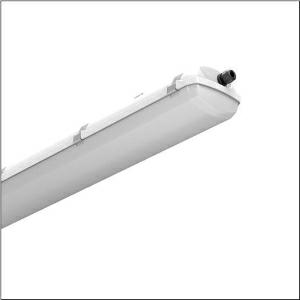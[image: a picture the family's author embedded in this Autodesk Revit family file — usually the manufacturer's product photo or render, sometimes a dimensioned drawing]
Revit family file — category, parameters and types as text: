
# Revit family: monsun_r__ex_51fxa27l460a_7d1b
name_source: partatom
category: Lighting Fixtures
units: mm (PartAtom-declared; Revit-internal decimal feet)

## family parameters
Cut with Voids When Loaded = No
Host = Face
Light Source = No
Part Type = Normal
Room Calculation Point = No
Round Connector Dimension = Use Diameter
Shared = No

## types (1)
- Monsun® Ex (1 x LED, 6560 lm, 53 W, 4000K)
    Apparent Load = 53 VA
    CIE Flux Codes = 46 76 94 98 100
    Color Rendering = 80
    Color Temperature = 4000K
    Default Elevation = 1800 mm
    Description = Monsun® Ex, damp-proof luminaire, primary optical cover: cover, of PC, UV-stabilised, opal, light emission: direct distribution, primary light characteristic: symmetric, installation type: surface-mounted, LED, rated luminous flux: 6.560lm, luminous efficacy: 124lm/W, light colour: 840, colour temperature: 4000K, control gear: ON/OFF, with terminal, 3-pole, max. 2.5mm², through-wiring: 5x 2.5mm², mains connection: 220..250V, AC, 50/60Hz, rated input power: 53W, housing, of PC, light grey (RAL 7035), incl. 1x Ex cable gland M20 for cable diameter 7..12mm with sealing, incl. 1x Ex locking screw M20 with sealing, length: 1.280mm, width: 155mm, height: 105mm, clip for enclosure, of stainless steel, protection rating (complete): IP66, insulation class (complete): insulation class I (protective earthing), certification: CE, explosion class: zone 1,21 II 2G Ex eb mb op is IIC T4 Gb, II 2D Ex tb op is IIIC T67°C Db, impact resistance: IK10, permissible operating ambient temperature: -20..+40°C, contact your sales advisor before using the luminaires in applications with unclear chemical exposure, large temperature fluctuations or condensation-forming humidity, packaging unit: 1 piece
    Height = 105 mm
    Lamp = 1 x LED
    Lamp Light Flux = 6560 lm
    Lamp Power = 53 W
    Lamp count = 1
    Length = 1280 mm
    Luminous efficacy = 124 lm/W
    Manufacturer = Siteco
    ModVariant = No
    Model = 51FXA27L460A
    Mounting Place = Ceiling
    Mounting Type = Surface mounted
    Number of Poles = 1
    OnlyDefault = Yes
    Power Factor = 1
    Product Name = Monsun® Ex
    Product group = damp-proof luminaire
    ProductGroupID = 300
    Protection Class = Protection class I
    Protection Degree = IP 66
    RLX_Detail_Level = 1
    RLX_Emergency_Light_Flux = 0 lm
    RLX_Emergency_Type = 0
    RLX_Emergency_Type_DB = No
    RlxData = <blob elided: 41557 chars, md5=ba2744e1>
    Socket = socket
    Standby Power = 0 W
    System Light Flux = 6560 lm
    System Power = 53 W
    Type Comments = Product without accessories
    Type Image = l_1258882.jpg
    URL = http://relux.com
    VarID = ---
    Voltage = 0 V
    Weight = 0.00 kg
    Width = 155 mm

## geometry (parser evidence)
native form markers: Blend x4, Sweep x12
no freeform markers — native parametric forms only
